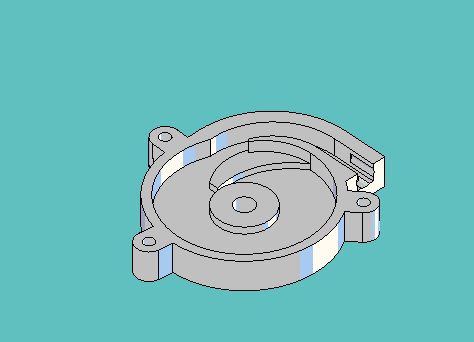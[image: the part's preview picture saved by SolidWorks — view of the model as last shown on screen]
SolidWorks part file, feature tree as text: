
SOLIDWORKS PART (.sldprt)
format: sldprt  version: not decoded by parser v0  size: 858,112 bytes
history: native  units: mm
features: sketch x11, extrude x8, cut_extrude x3, plane x3, material x1, chamfer x1 (+11 scaffold rows collapsed)
feature tree (38):
  scaffold x11  (default folders/planes/origin — collapsed)
  material  "Material <not specified>"
  sketch  "Sketch1"  dims[D1=6.35mm D2=60.325mm]
  extrude  "Extrude1"  Depth=4.7625mm
  sketch  "Sketch2"  dims[D1=3.175mm]
  extrude  "Extrude2"  Depth=2.286mm
  sketch  "Sketch3"  dims[c1.D4=7.9375mm c1.D6=31.75mm c1.D8=~16.03375mm c2.D6=25.4mm c2.D1=~17.512839mm c3.D1=45.0deg c3.D2=~14.559872mm c3.D3=4.7625mm c3.D5=19.05mm c3.D7=3.175mm]
  extrude  "Extrude3"  [1 undecoded]
  sketch  "Sketch4"  dims[D1=6.35mm]
  cut_extrude  "Cut-Extrude1"  [1 undecoded]
  sketch  "Sketch5"  dims[c1.D2=48.26mm c1.D3=19.05mm c2.D2=~1.749908mm c3.D2=43.0deg c3.D1=0.0mm]
  extrude  "Extrude4"  Depth=4.16052mm
  sketch  "Sketch7"  dims[c1.D2=~37.848969mm c1.D1=4.7625mm c2.D2=4.7625mm c2.D3=6.35mm c2.D1=39.878mm c3.D2=3.175mm]
  extrude  "Extrude6"  [1 undecoded]
  sketch  "Sketch8"
  extrude  "Extrude7"  [1 undecoded]
  sketch  "Sketch9"  dims[D1=~7.14375mm D2=3.175mm D3=3.175mm]
  cut_extrude  "Cut-Extrude2"  Depth=9.525mm
  sketch  "Sketch10"  dims[c1.D3=3.7338mm c1.D6=3.7338mm c1.D9=3.7338mm c1.D7=69.85mm c1.D12=4.7625mm c1.D5=~3.96875mm c2.D12=~3.96875mm c2.D1=4.7625mm c2.D2=4.7625mm c2.D4=~69.703815mm c3.D4=120.0deg c3.D5=4.7625mm c3.D6=4.7625mm c3.D7=~69.703815mm c4.D7=120.0deg c4.D8=~3.96875mm c5.D7=~49.394425mm c6.D7=120.0deg c6.D4=~49.394425mm c7.D4=130.0deg c7.D7=~46.980774mm c8.D7=77.0deg c8.D10=~49.394425mm c9.D10=120.0deg c9.D1=~107.458775mm c10.D1=163.0deg c10.D2=4.7625mm c10.D10=~49.394425mm c11.D10=137.0deg c11.D11=~49.394425mm c12.D11=137.0deg c12.D2=~3.96875mm]
  extrude  "Extrude8"  [1 undecoded]
  sketch  "Sketch11"  dims[D1=20.32mm]
  extrude  "Extrude9"  Depth=2.667mm
  chamfer  "Chamfer1"  Distance=1.5875mm Angle=45deg
  sketch  "Sketch12"  dims[D2=2.7051mm D1=4.7625mm D3=3.175mm]
  cut_extrude  "Cut-Extrude3"  [1 undecoded]
  plane  "Plane2"
  plane  "Plane3"  Offset=0mm
  plane  "Plane4"
decode coverage: 16 of 23 modeling features carry decoded parameters
note: ~ marks probable driven/reference dimensions
note: 6 parameter values undecoded
summary: no parameter record found for 6 features
note: suppression state not decoded; provenance and decode notes live in map.json
